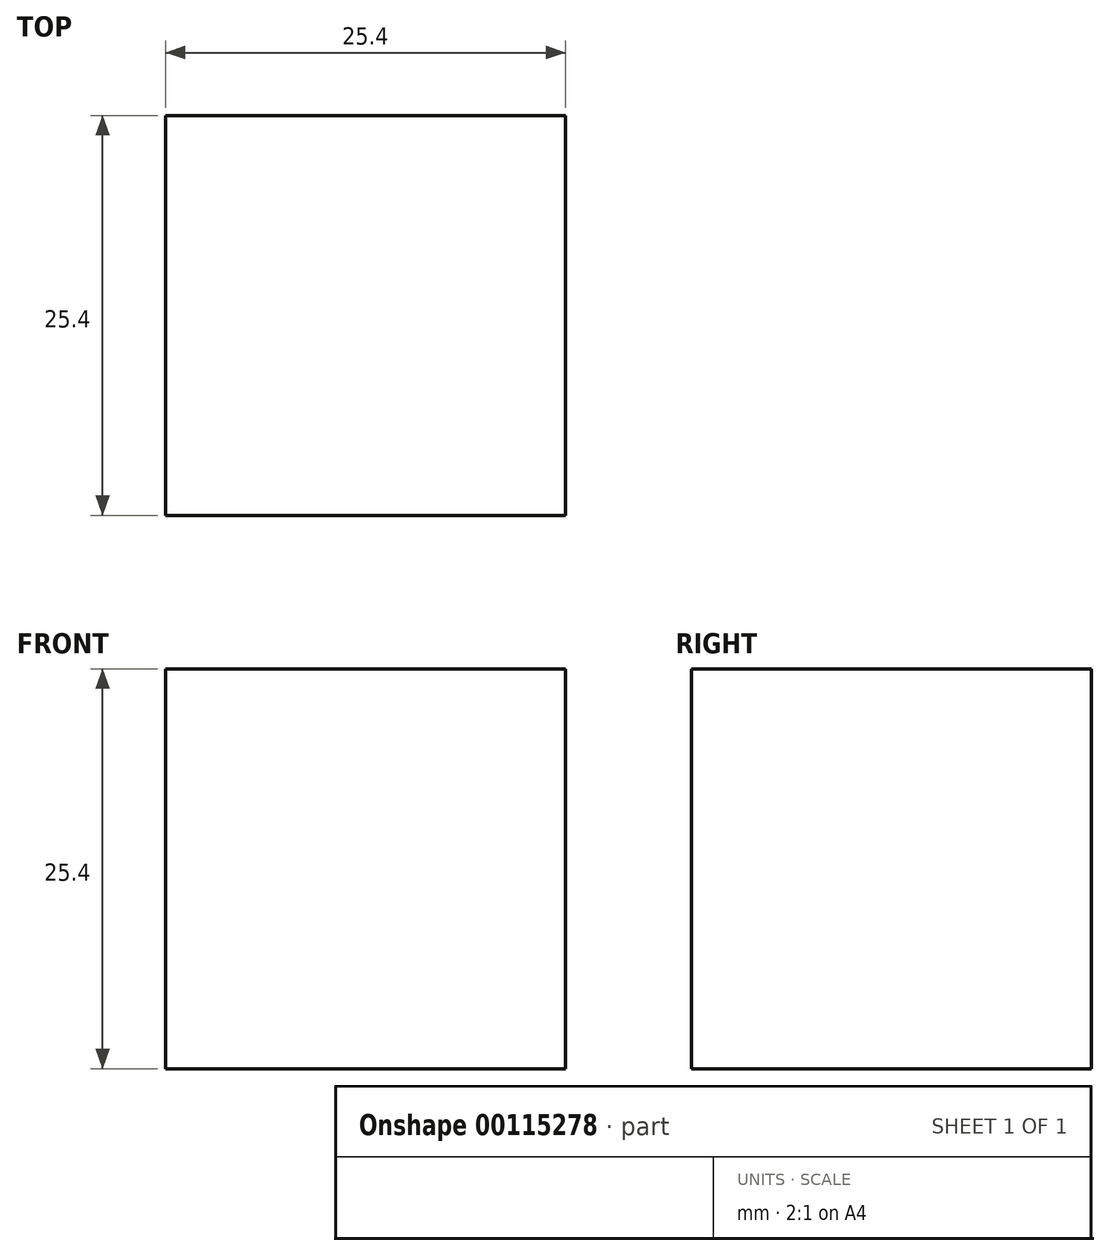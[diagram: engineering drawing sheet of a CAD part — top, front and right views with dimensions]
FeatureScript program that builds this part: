
annotation { "Feature Type Name" : "Feature", "Feature Type Description" : "" }
export const myFeature = defineFeature(function(context is Context, id is Id, definition is map)
    precondition{}
    {
        {
            var Q0;
            Q0=qCreatedBy(makeId("Top.planeOp"),FACE);
            var sketch = newSketch(context, id + "F0", { "sketchPlane" : qUnion([Q0])});
            skLineSegment(sketch, "E0.bottom", {"start": v(-17.66, -2.06) * mm, "end": v(-43.06, -2.06) * mm});
            skLineSegment(sketch, "E0.top", {"start": v(-17.66, 23.34) * mm, "end": v(-43.06, 23.34) * mm});
            skLineSegment(sketch, "E0.left", {"start": v(-17.66, -2.06) * mm, "end": v(-17.66, 23.34) * mm});
            skLineSegment(sketch, "E0.right", {"start": v(-43.06, -2.06) * mm, "end": v(-43.06, 23.34) * mm});
            skSolve(sketch);
        }
        {
            var Q0;
            Q0=makeQuery(id+"F0.imprint","IMPRINT",FACE,{"disambiguationData":[TD([[makeQuery(id+"F0.imprint","IMPRINT",EDGE,{"derivedFrom":sQuery(id+"F0.wireOp",EDGE,"E0.bottom")}),-1.0]])]});
            extrude(context, id + "F1", {"entities" : qUnion([Q0]), "depth" : 25.4 * mm});
        }
    });
